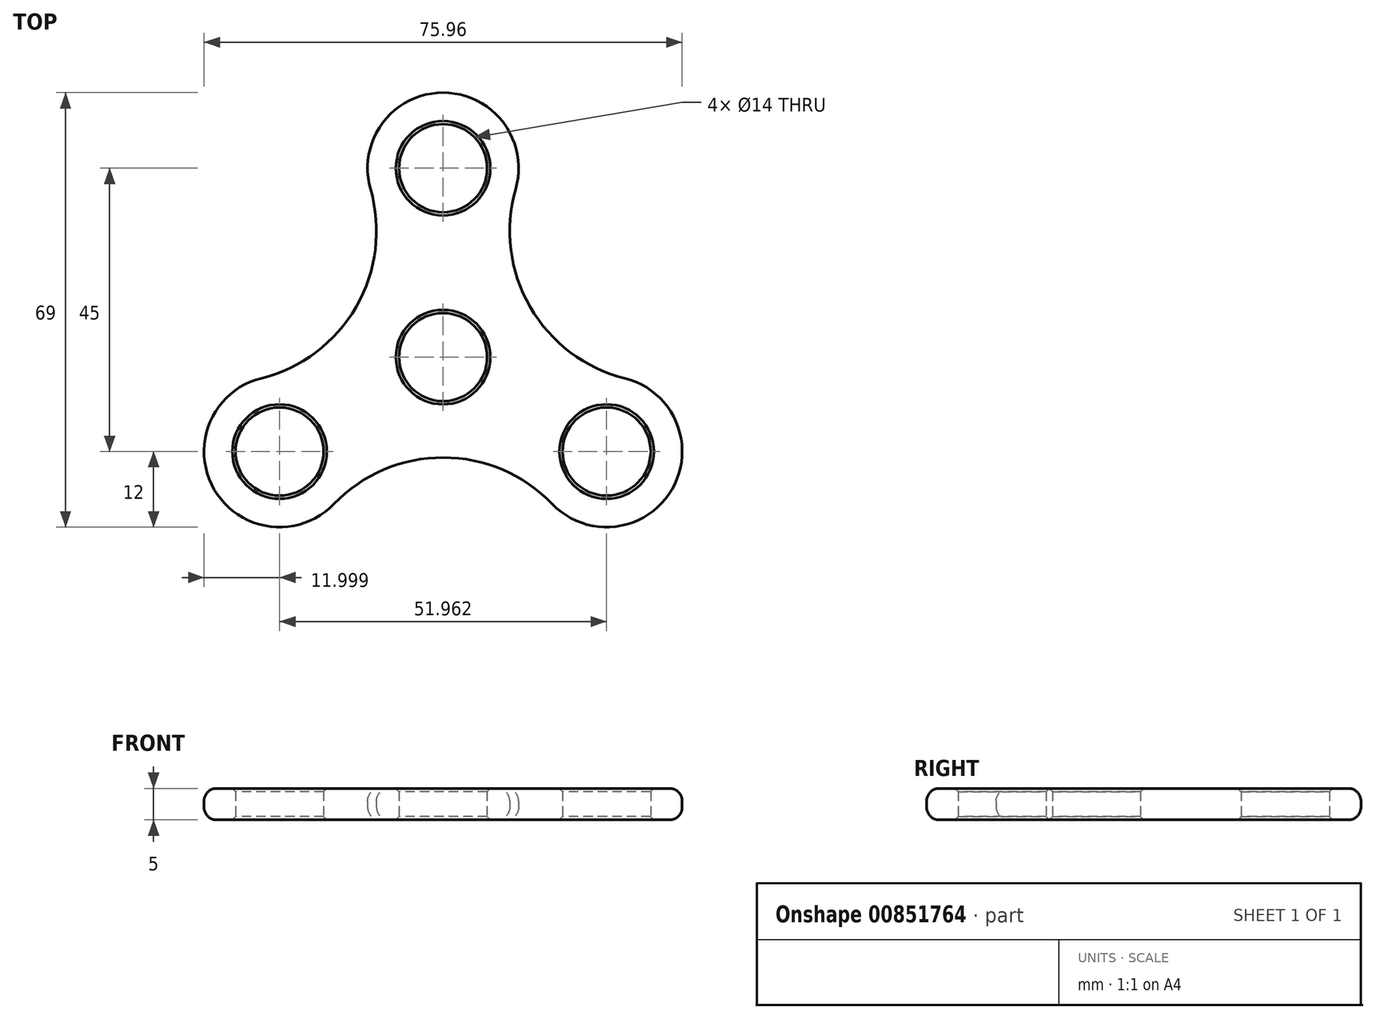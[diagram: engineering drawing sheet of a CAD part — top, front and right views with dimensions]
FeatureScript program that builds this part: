
annotation { "Feature Type Name" : "Feature", "Feature Type Description" : "" }
export const myFeature = defineFeature(function(context is Context, id is Id, definition is map)
    precondition{}
    {
        {
            var Q0;
            Q0=qCreatedBy(makeId("Top.planeOp"),FACE);
            var sketch = newSketch(context, id + "F0", { "sketchPlane" : qUnion([Q0])});
            skCircle(sketch, "E0", {"center": v(0, 0) * mm, "radius": 7 * mm});
            skCircle(sketch, "E1", {"center": v(0, 30) * mm, "radius": 7 * mm});
            skCircle(sketch, "E2.1.0", {"center": v(-25.98, -15) * mm, "radius": 7 * mm});
            skCircle(sketch, "E2.2.0", {"center": v(25.98, -15) * mm, "radius": 7 * mm});
            skArc(sketch, "E3.0", {"start": v(11.53, 26.68) * mm, "mid": v(0, 42) * mm, "end": v(-11.53, 26.68) * mm});
            skArc(sketch, "E4.0", {"start": v(-28.87, -3.35) * mm, "mid": v(-36.37, -21) * mm, "end": v(-17.34, -23.33) * mm});
            skArc(sketch, "E5.0", {"start": v(17.34, -23.33) * mm, "mid": v(36.37, -21) * mm, "end": v(28.87, -3.35) * mm});
            skArc(sketch, "E6", {"start": v(11.53, 26.68) * mm, "mid": v(13.82, 7.98) * mm, "end": v(28.87, -3.35) * mm});
            skArc(sketch, "E7.1.0", {"start": v(-28.87, -3.35) * mm, "mid": v(-13.82, 7.98) * mm, "end": v(-11.53, 26.68) * mm});
            skArc(sketch, "E7.2.0", {"start": v(17.34, -23.33) * mm, "mid": v(0, -15.96) * mm, "end": v(-17.34, -23.33) * mm});
            skPoint(sketch, "E8.start.orphan", {"position": v(10.4, 36) * mm});
            skPoint(sketch, "E9.start.orphan", {"position": v(23.38, 13.5) * mm});
            skPoint(sketch, "E10.orphan", {"position": v(36.37, -9) * mm});
            skSolve(sketch);
        }
        {
            var Q0;
            Q0=makeQuery(id+"F0.imprint","IMPRINT",FACE,{"disambiguationData":[TD([[makeQuery(id+"F0.imprint","IMPRINT",EDGE,{"derivedFrom":sQuery(id+"F0.wireOp",EDGE,"E0")}),-1.0]])]});
            extrude(context, id + "F1", {"entities" : qUnion([Q0]), "endBound" : BoundingType.SYMMETRIC, "depth" : 5 * mm, "offsetDistance" : 25 * mm});
        }
        {
            var Q0;
            Q0=makeQuery(id+"F1.opExtrude","CAP_EDGE",EDGE,{"disambiguationData":[OSD([sQuery(id+"F0.wireOp",EDGE,"E7.2.0")])],"isStart":false});
            var Q1;
            Q1=makeQuery(id+"F1.opExtrude","CAP_EDGE",EDGE,{"disambiguationData":[OSD([sQuery(id+"F0.wireOp",EDGE,"E6")])],"isStart":true});
            fillet(context, id + "F2", {"entities" : qUnion([Q0, Q1]), "radius" : 2 * mm, "tangentPropagation" : true, "allowEdgeOverflow" : false});
        }
        {
            var Q0;
            Q0=makeQuery(id+"F1.opExtrude","CAP_EDGE",EDGE,{"disambiguationData":[OSD([sQuery(id+"F0.wireOp",EDGE,"E2.1.0")])],"isStart":false});
            var Q1;
            Q1=makeQuery(id+"F1.opExtrude","CAP_EDGE",EDGE,{"disambiguationData":[OSD([sQuery(id+"F0.wireOp",EDGE,"E0")])],"isStart":false});
            var Q2;
            Q2=makeQuery(id+"F1.opExtrude","CAP_EDGE",EDGE,{"disambiguationData":[OSD([sQuery(id+"F0.wireOp",EDGE,"E2.2.0")])],"isStart":false});
            var Q3;
            Q3=makeQuery(id+"F1.opExtrude","CAP_EDGE",EDGE,{"disambiguationData":[OSD([sQuery(id+"F0.wireOp",EDGE,"E1")])],"isStart":false});
            var Q4;
            Q4=makeQuery(id+"F1.opExtrude","CAP_EDGE",EDGE,{"disambiguationData":[OSD([sQuery(id+"F0.wireOp",EDGE,"E0")])],"isStart":true});
            var Q5;
            Q5=makeQuery(id+"F1.opExtrude","CAP_EDGE",EDGE,{"disambiguationData":[OSD([sQuery(id+"F0.wireOp",EDGE,"E2.2.0")])],"isStart":true});
            var Q6;
            Q6=makeQuery(id+"F1.opExtrude","CAP_EDGE",EDGE,{"disambiguationData":[OSD([sQuery(id+"F0.wireOp",EDGE,"E2.1.0")])],"isStart":true});
            var Q7;
            Q7=makeQuery(id+"F1.opExtrude","CAP_EDGE",EDGE,{"disambiguationData":[OSD([sQuery(id+"F0.wireOp",EDGE,"E1")])],"isStart":true});
            chamfer(context, id + "F3", {"entities" : qUnion([Q0, Q1, Q2, Q3, Q4, Q5, Q6, Q7]), "width" : .5 * mm, "tangentPropagation" : true});
        }
    });
